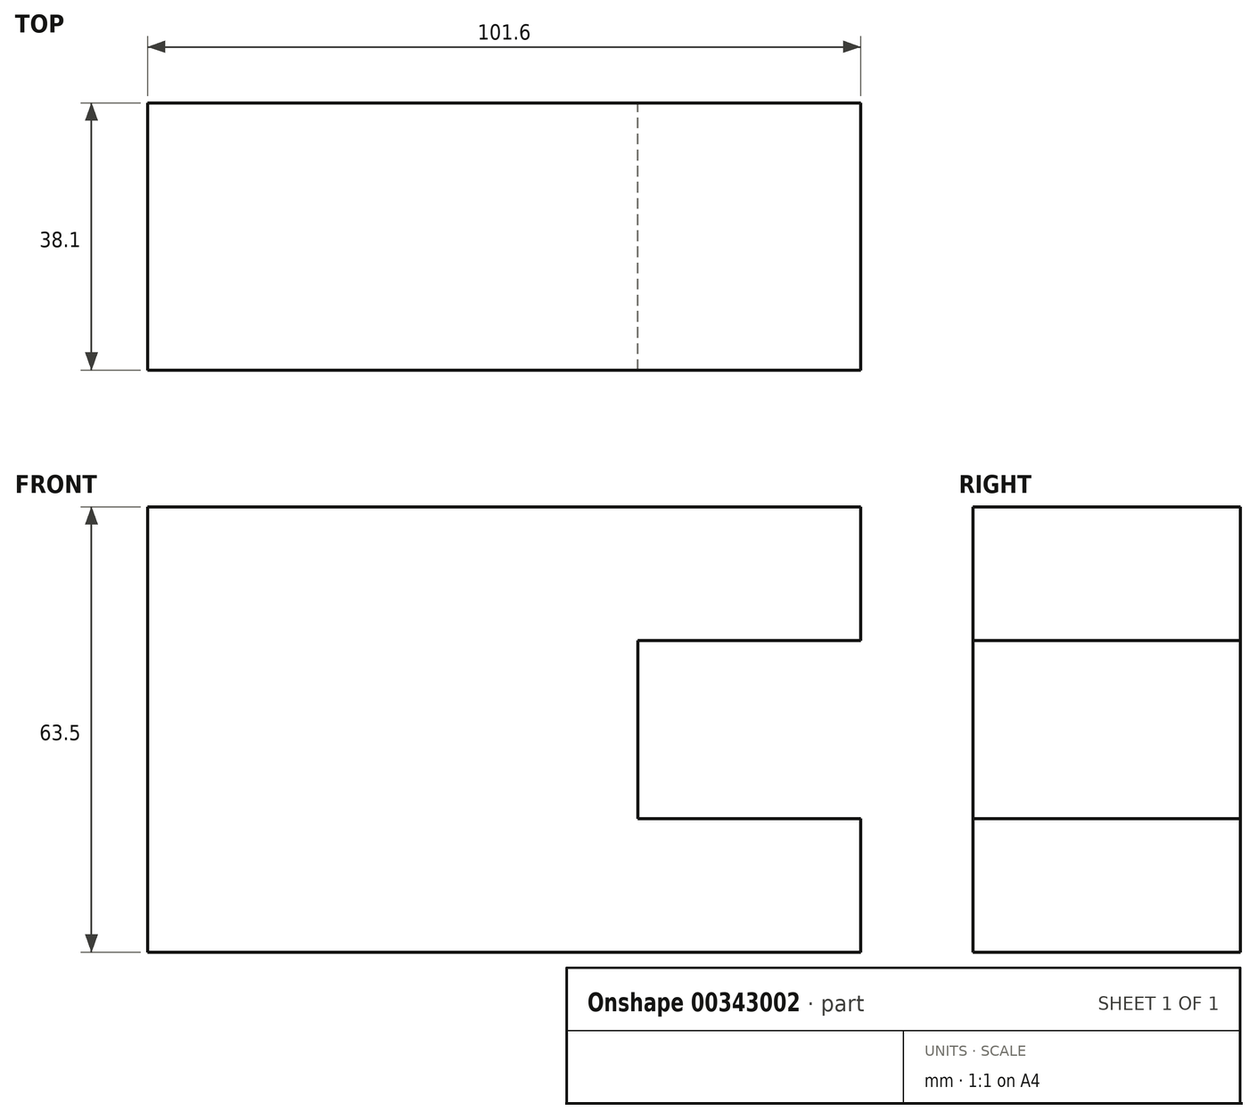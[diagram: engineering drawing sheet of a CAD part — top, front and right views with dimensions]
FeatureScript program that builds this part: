
annotation { "Feature Type Name" : "Feature", "Feature Type Description" : "" }
export const myFeature = defineFeature(function(context is Context, id is Id, definition is map)
    precondition{}
    {
        {
            var Q0;
            Q0=qCreatedBy(makeId("Front.planeOp"),FACE);
            var sketch = newSketch(context, id + "F0", { "sketchPlane" : qUnion([Q0])});
            skLineSegment(sketch, "E0", {"start": v(45.22, -24.2) * mm, "end": v(-56.38, -24.2) * mm});
            skLineSegment(sketch, "E1", {"start": v(-56.38, -24.2) * mm, "end": v(-56.38, 39.3) * mm});
            skLineSegment(sketch, "E2", {"start": v(-56.38, 39.3) * mm, "end": v(45.22, 39.3) * mm});
            skLineSegment(sketch, "E3", {"start": v(45.22, 39.3) * mm, "end": v(45.22, 20.25) * mm});
            skLineSegment(sketch, "E4", {"start": v(45.22, 20.25) * mm, "end": v(13.47, 20.25) * mm});
            skLineSegment(sketch, "E5", {"start": v(13.47, 20.25) * mm, "end": v(13.47, -5.15) * mm});
            skLineSegment(sketch, "E6", {"start": v(13.47, -5.15) * mm, "end": v(45.22, -5.15) * mm});
            skLineSegment(sketch, "E7", {"start": v(45.22, -5.15) * mm, "end": v(45.22, -24.2) * mm});
            skSolve(sketch);
        }
        {
            var Q0;
            Q0 = qSketchRegion(id + "F0", true);
            extrude(context, id + "F1", {"entities" : qUnion([Q0]), "depth" : 38.1 * mm});
        }
    });
